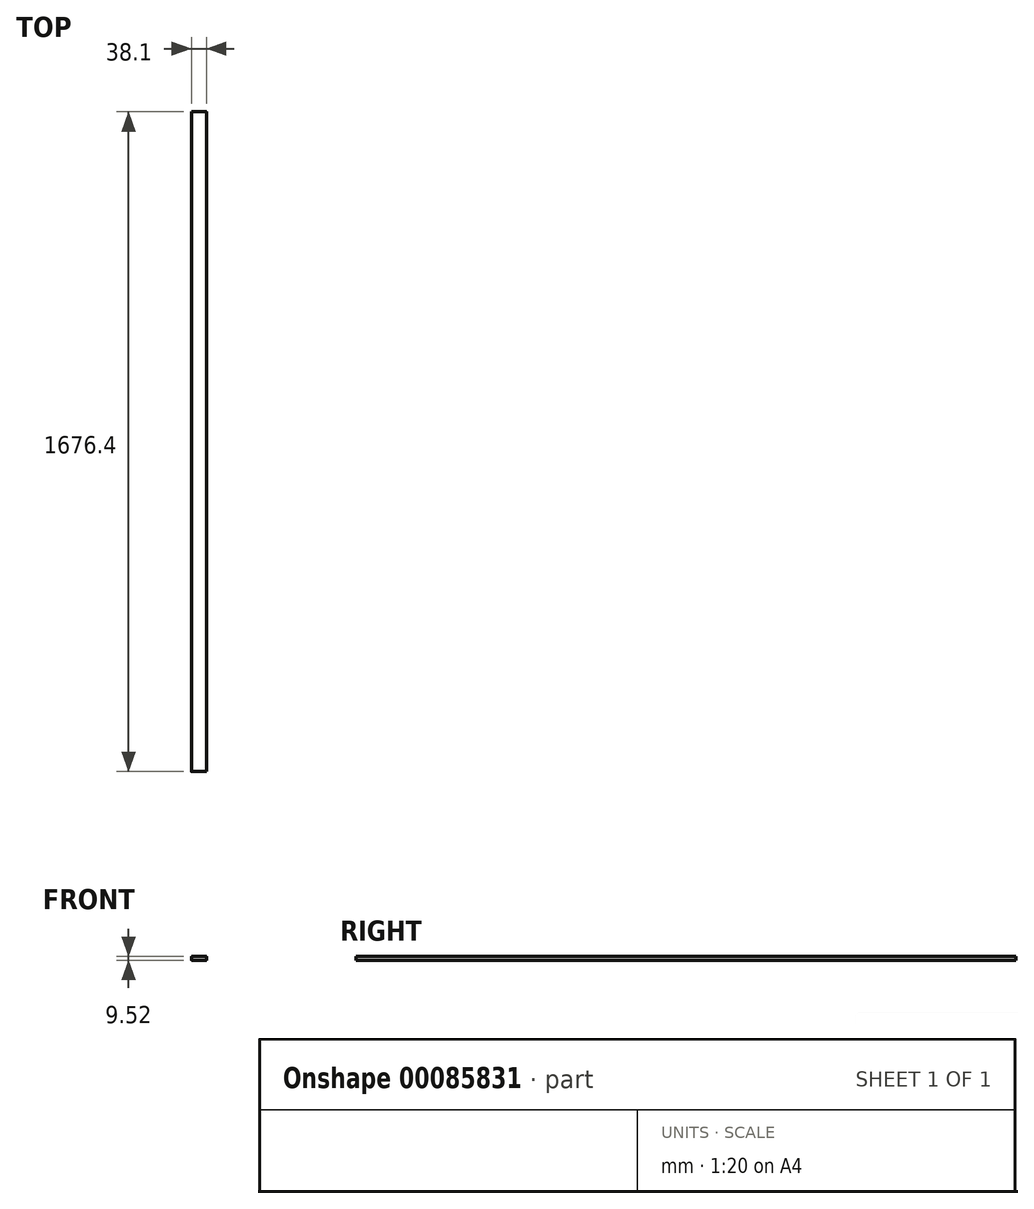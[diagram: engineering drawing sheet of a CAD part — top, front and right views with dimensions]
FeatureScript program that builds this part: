
annotation { "Feature Type Name" : "Feature", "Feature Type Description" : "" }
export const myFeature = defineFeature(function(context is Context, id is Id, definition is map)
    precondition{}
    {
        {
            var Q0;
            Q0=qCreatedBy(makeId("Front.planeOp"),FACE);
            var sketch = newSketch(context, id + "F0", { "sketchPlane" : qUnion([Q0])});
            skLineSegment(sketch, "E0.bottom", {"start": v(-46.07, 62.47) * mm, "end": v(-9.55, 62.47) * mm});
            skLineSegment(sketch, "E0.top", {"start": v(-46.07, 52.95) * mm, "end": v(-9.55, 52.95) * mm});
            skLineSegment(sketch, "E0.left", {"start": v(-46.86, 61.69) * mm, "end": v(-46.86, 53.74) * mm});
            skLineSegment(sketch, "E0.right", {"start": v(-8.76, 61.69) * mm, "end": v(-8.76, 53.74) * mm});
            skPoint(sketch, "E1.visualSharp", {"position": v(-46.86, 62.47) * mm});
            skArc(sketch, "E1.filletArc", {"start": v(-46.07, 62.47) * mm, "mid": v(-46.63, 62.24) * mm, "end": v(-46.86, 61.69) * mm});
            skPoint(sketch, "E2.visualSharp", {"position": v(-46.86, 52.95) * mm});
            skArc(sketch, "E2.filletArc", {"start": v(-46.86, 53.74) * mm, "mid": v(-46.63, 53.18) * mm, "end": v(-46.07, 52.95) * mm});
            skPoint(sketch, "E3.visualSharp", {"position": v(-8.76, 62.47) * mm});
            skArc(sketch, "E3.filletArc", {"start": v(-8.76, 61.69) * mm, "mid": v(-8.99, 62.24) * mm, "end": v(-9.55, 62.47) * mm});
            skPoint(sketch, "E4.visualSharp", {"position": v(-8.76, 52.95) * mm});
            skArc(sketch, "E4.filletArc", {"start": v(-9.55, 52.95) * mm, "mid": v(-8.99, 53.18) * mm, "end": v(-8.76, 53.74) * mm});
            skSolve(sketch);
        }
        {
            var Q0;
            Q0=makeQuery(id+"F0.imprint","IMPRINT",FACE,{"disambiguationData":[TD([[makeQuery(id+"F0.imprint","IMPRINT",EDGE,{"derivedFrom":sQuery(id+"F0.wireOp",EDGE,"E0.bottom")}),-1.0]])]});
            extrude(context, id + "F1", {"entities" : qUnion([Q0]), "depth" : 1676.4 * mm, "offsetDistance" : 25.4 * mm});
        }
    });
